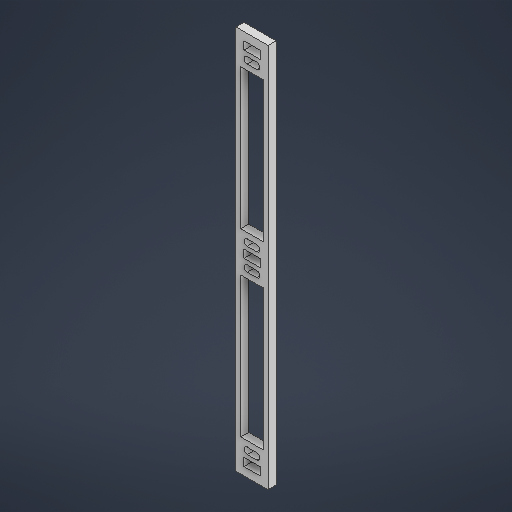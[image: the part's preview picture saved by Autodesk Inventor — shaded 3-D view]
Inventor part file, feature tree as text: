
AUTODESK INVENTOR PART (.ipt)
format: ipt  version: 2025.3 (Build 293356000, 356)  size: 316,416 bytes
history: native  units: mm
features: extrude x1, sketch x1
ambient origin geometry x8: Origin, YZ Plane, XZ Plane, XY Plane, X Axis, Y Axis, Z Axis, Center Point
bodies: Body1 (feature_tree)
feature tree (2):
  extrude  "Extrusion3"  Depth=20.0mm
  sketch  "Sketch1"  dims[d0=240.0mm d1=20.0mm d2=10.0mm d3=5.0mm d4=107.5mm d5=5.0mm d6=5.0mm d7=5.0mm d10=2.0mm d11=2.5mm d12=7.0mm d13=7.0mm d14=2.5mm d15=2.0mm d16=7.0mm d17=7.0mm d18=2.0mm d19=6.0mm d20=7.0mm d21=2.5mm d22=2.5mm d23=2.0mm d24=7.0mm d25=7.0mm d28=3.5mm d29=3.5mm d30=3.0mm d31=3.0mm d32=3.5mm d33=3.5mm d34=3.0mm d35=3.0mm d36=5.0mm d37=0.0mm]
